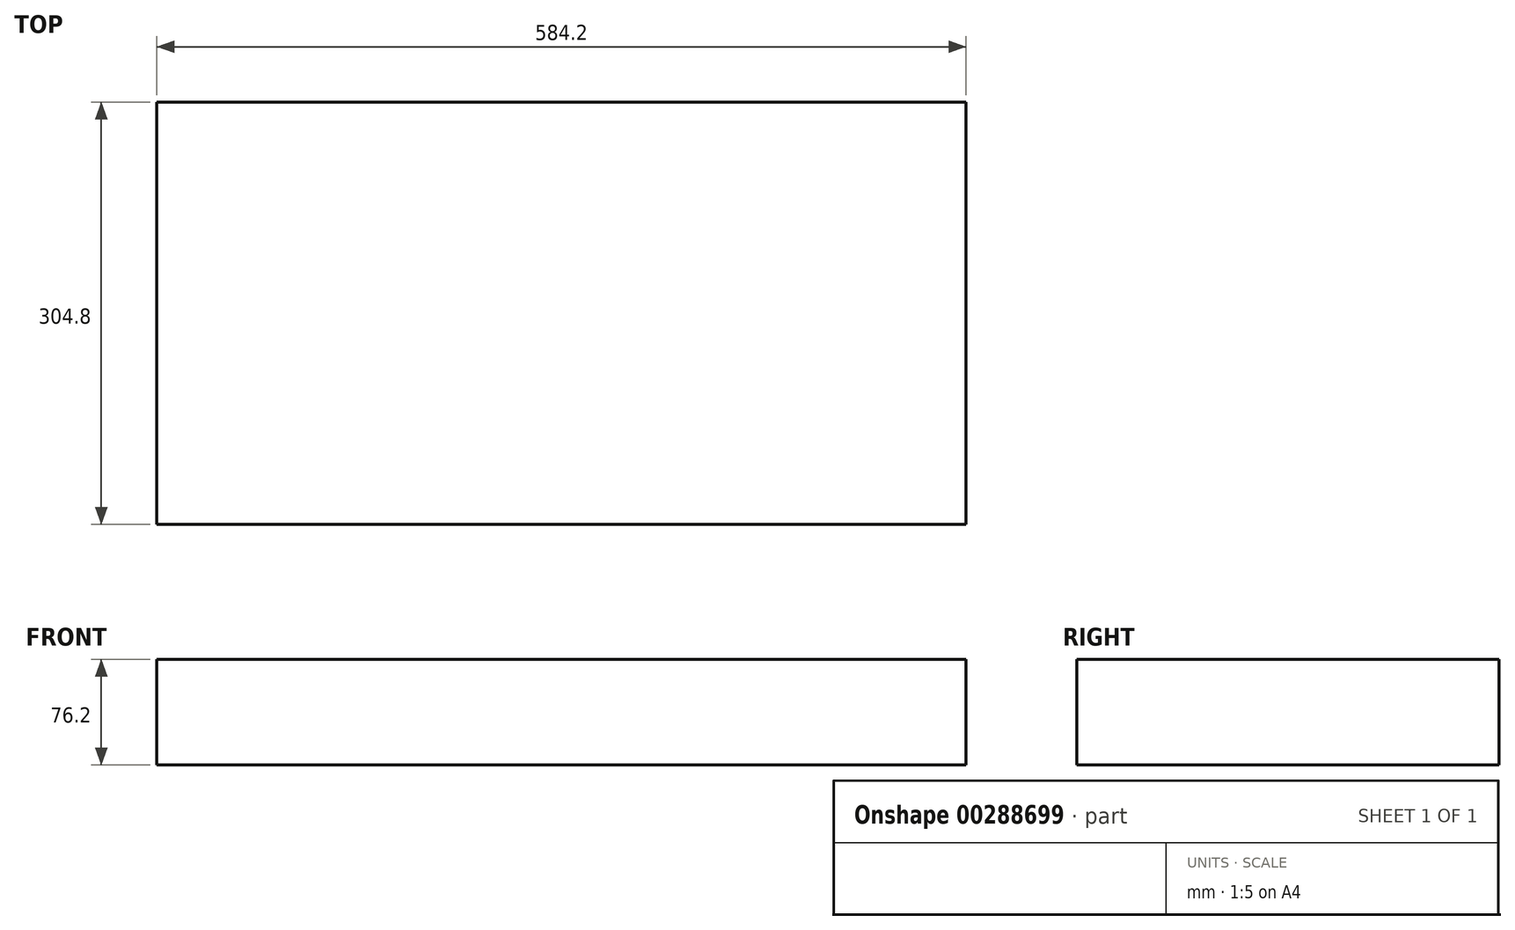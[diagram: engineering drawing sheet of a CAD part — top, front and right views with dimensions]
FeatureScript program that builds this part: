
annotation { "Feature Type Name" : "Feature", "Feature Type Description" : "" }
export const myFeature = defineFeature(function(context is Context, id is Id, definition is map)
    precondition{}
    {
        {
            var Q0;
            Q0=qCreatedBy(makeId("Top.planeOp"),FACE);
            var sketch = newSketch(context, id + "F0", { "sketchPlane" : qUnion([Q0])});
            skLineSegment(sketch, "E0.bottom", {"start": v(292.1, 152.4) * mm, "end": v(-292.1, 152.4) * mm});
            skLineSegment(sketch, "E0.top", {"start": v(292.1, -152.4) * mm, "end": v(-292.1, -152.4) * mm});
            skLineSegment(sketch, "E0.left", {"start": v(292.1, 152.4) * mm, "end": v(292.1, -152.4) * mm});
            skLineSegment(sketch, "E0.right", {"start": v(-292.1, 152.4) * mm, "end": v(-292.1, -152.4) * mm});
            skPoint(sketch, "E0.middle", {"position": v(0, 0) * mm});
            skSolve(sketch);
        }
        {
            var Q0;
            Q0=qSketchRegion(id+"F0",true);
            extrude(context, id + "F1", {"entities" : qUnion([Q0]), "endBound" : BoundingType.SYMMETRIC, "depth" : 76.2 * mm});
        }
    });
